# Revit family: 303_R401HX_+R460H
name_source: partatom
category: Pipe Accessories
revit_build: Autodesk Revit 2018 (Build: 20170223_1515(x64)
units: mm (PartAtom-declared; Revit-internal decimal feet)

## family parameters
Always vertical = Yes
Cut with Voids When Loaded = No
Part Type = Valve - Breaks Into
Round Connector Dimension = Use Diameter
Shared = No
Work Plane-Based = No

## types (2) — shared parameters
CAT0 = Yes
CenSd_TR_6 = 16 mm
Description = Angle valve with thermostatic option
H3 = 7 mm  [stored 0.0229659 ft]
H3__ve = -7 mm
H4 = 3 mm  [stored 0.00984252 ft]
H4__ve = -3 mm
J2 = 2 mm  [stored 0.00656168 ft]
J4 = 2 mm  [stored 0.00656168 ft]
L2D_Min = 3048 mm  [stored 10 ft]
M3 = 19 mm  [stored 0.062336 ft]
M3__ve = -19 mm  [stored -0.062336 ft]
Manufacturer = Giacomini
QmdConnectorList = 301;D;302;D1
THR1 = 4 mm  [stored 0.0131234 ft]
TR = 19 mm  [stored 0.062336 ft]
TR1 = 15 mm  [stored 0.0492126 ft]
URL = http://www.giacomini.com
X1 = 19 mm  [stored 0.062336 ft]
magiPartTypeId = 303
magiProductFamilyId = R401HX*+R460H
zero-valued in all types: MC_Default_elevation

## per-type parameters (varying)
| type | B1 | B2 | B3 | B4 | CenSd_K1_6 | CenSd_W2_6 | D | D1 | J | J3 | K1 | KH | KH__ve | L | L1 | L2D | L5 | LX | R1 | THR | W1 | W2 | W2D | W3 |
| R401HX003+R460H | 7 mm  [stored 0.0229659 ft] | 8 mm  [stored 0.0262467 ft] | 11 mm | 11 mm | 12 mm  [stored 0.0393701 ft] | 13 mm | 15 mm | 15 mm | 27 mm  [stored 0.0885827 ft] | 9 mm  [stored 0.0295276 ft] | 14 mm  [stored 0.0459318 ft] | 11 mm | -11 mm | 44 mm  [stored 0.144357 ft] | 11 mm | 44 mm  [stored 0.144357 ft] | 13 mm | 59 mm | 8 mm  [stored 0.0262467 ft] | 70 mm | 12 mm  [stored 0.0393701 ft] | 15 mm  [stored 0.0492126 ft] | 15 mm  [stored 0.0492126 ft] | 9 mm  [stored 0.0295276 ft] |
| R401HX004+R460H | 8 mm  [stored 0.0262467 ft] | 10 mm  [stored 0.0328084 ft] | 13 mm | 14 mm  [stored 0.0459318 ft] | 14 mm  [stored 0.0459318 ft] | 16 mm | 20 mm | 20 mm | 29 mm | 10 mm  [stored 0.0328084 ft] | 16 mm | 12 mm  [stored 0.0393701 ft] | -12 mm  [stored -0.0393701 ft] | 50 mm  [stored 0.164042 ft] | 14 mm  [stored 0.0459318 ft] | 50 mm  [stored 0.164042 ft] | 15 mm  [stored 0.0492126 ft] | 67 mm | 10 mm  [stored 0.0328084 ft] | 71 mm | 15 mm  [stored 0.0492126 ft] | 19 mm  [stored 0.062336 ft] | 20 mm  [stored 0.0656168 ft] | 11 mm |

note: column(s) folded — value = type name in every type: magiProductCode, magiProductId

note: [stored X ft] marks values corroborated as IEEE doubles in the binary element streams (Revit-internal decimal feet)

## geometry (parser evidence)
native form markers: Sweep x2
no freeform markers — native parametric forms only
